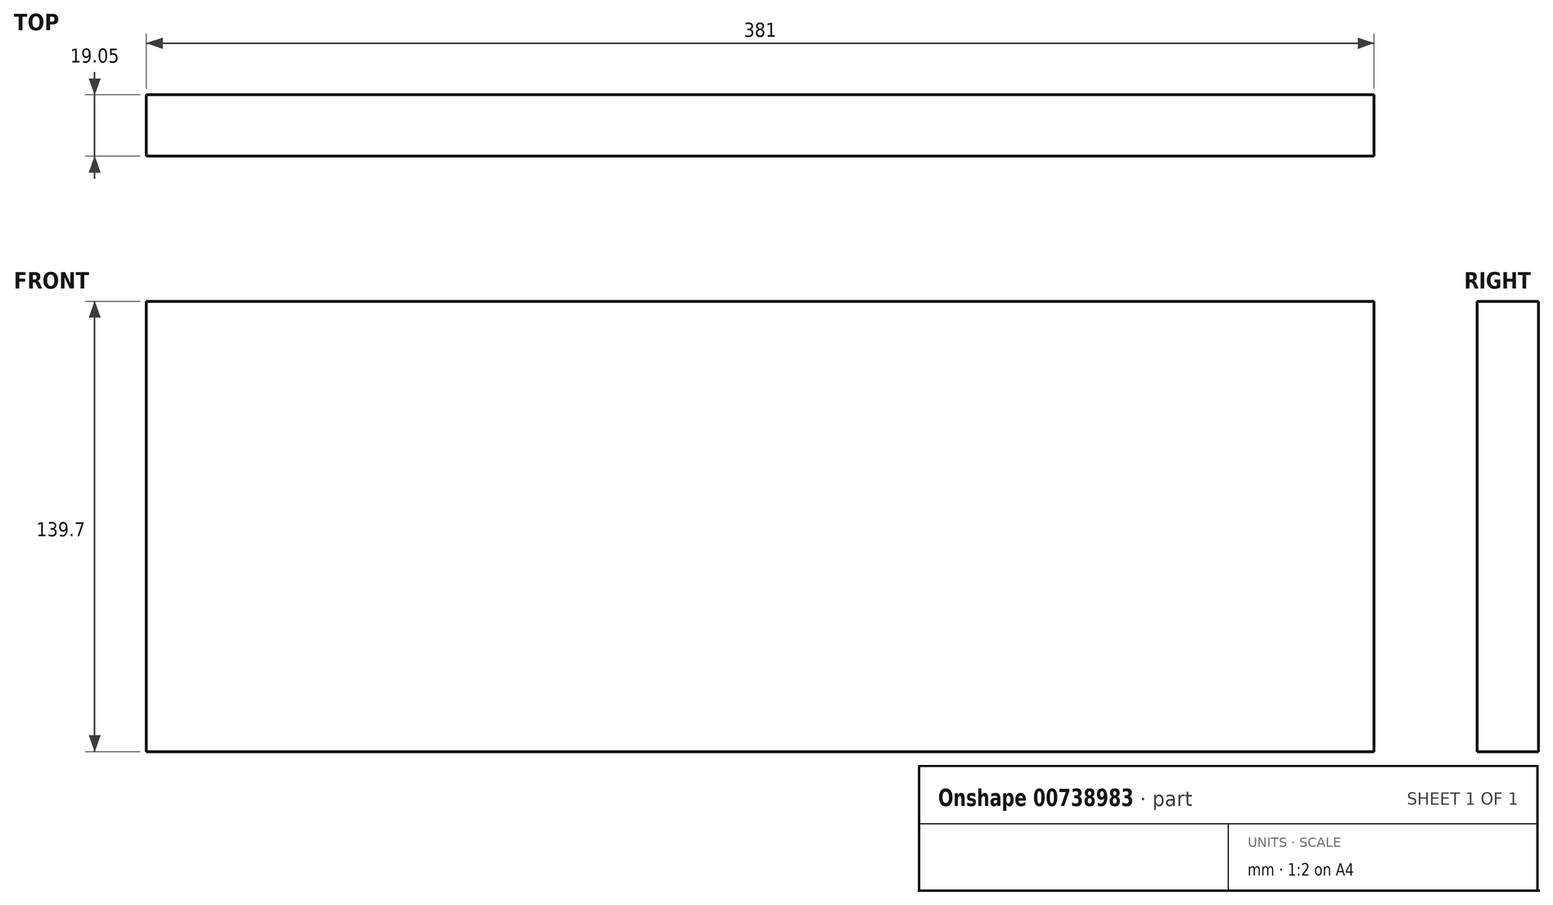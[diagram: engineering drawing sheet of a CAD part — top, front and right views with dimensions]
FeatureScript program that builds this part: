
annotation { "Feature Type Name" : "Feature", "Feature Type Description" : "" }
export const myFeature = defineFeature(function(context is Context, id is Id, definition is map)
    precondition{}
    {
        {
            var Q0;
            Q0=qCreatedBy(makeId("Front.planeOp"),FACE);
            var sketch = newSketch(context, id + "F0", { "sketchPlane" : qUnion([Q0])});
            skLineSegment(sketch, "E0.bottom", {"start": v(-203.88, 85.7) * mm, "end": v(177.12, 85.7) * mm});
            skLineSegment(sketch, "E0.top", {"start": v(-203.88, -54) * mm, "end": v(177.12, -54) * mm});
            skLineSegment(sketch, "E0.left", {"start": v(-203.88, 85.7) * mm, "end": v(-203.88, -54) * mm});
            skLineSegment(sketch, "E0.right", {"start": v(177.12, 85.7) * mm, "end": v(177.12, -54) * mm});
            skSolve(sketch);
        }
        {
            var Q0;
            Q0=makeQuery(id+"F0.imprint","IMPRINT",FACE,{"disambiguationData":[TD([[makeQuery(id+"F0.imprint","IMPRINT",EDGE,{"derivedFrom":sQuery(id+"F0.wireOp",EDGE,"E0.bottom")}),-1.0]])]});
            extrude(context, id + "F1", {"entities" : qUnion([Q0]), "depth" : 19.05 * mm, "offsetDistance" : 25.4 * mm});
        }
    });
